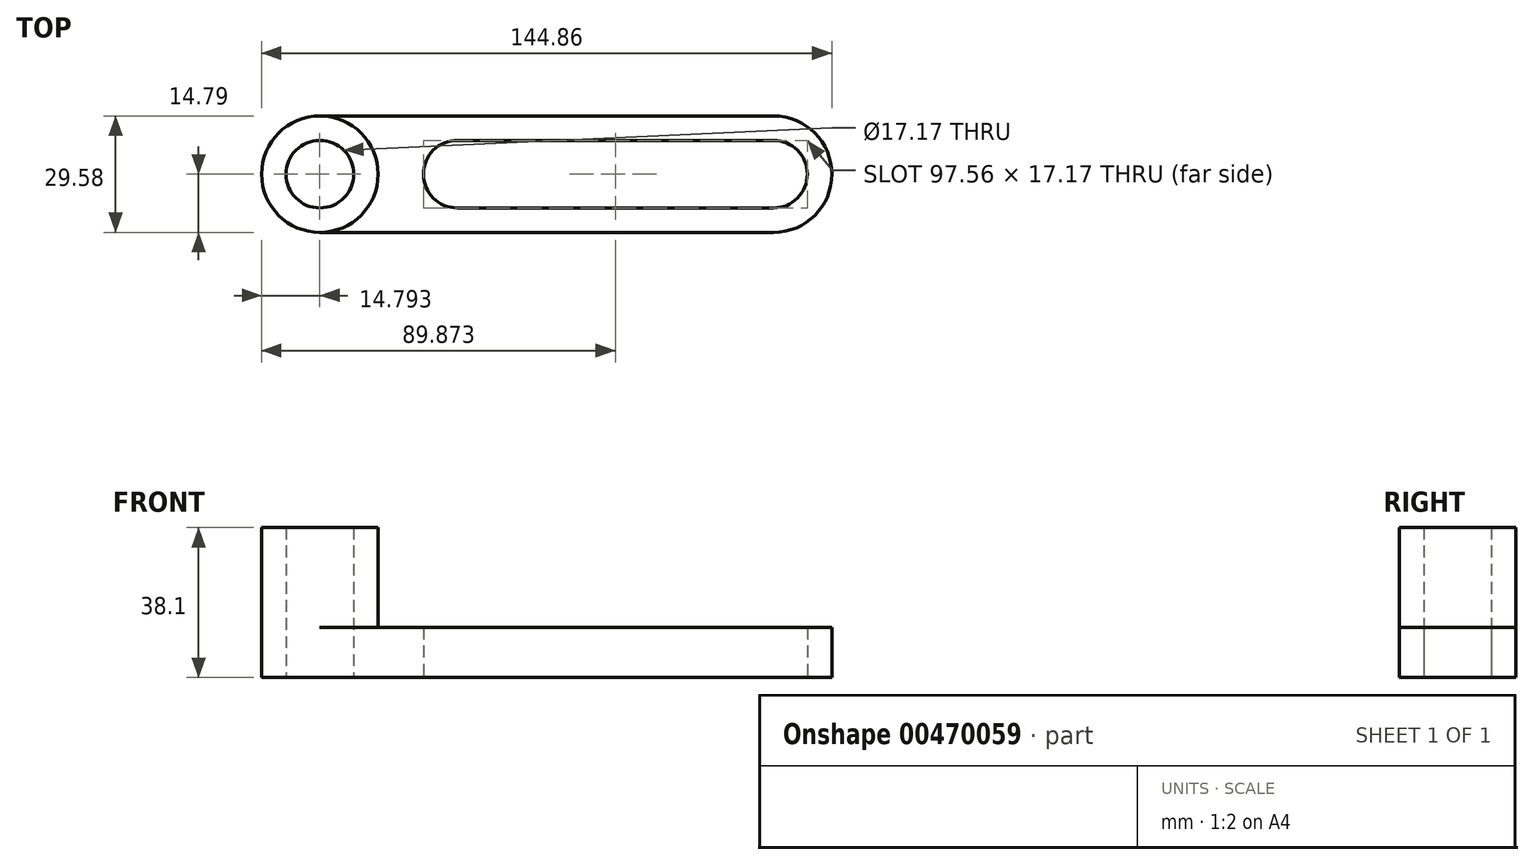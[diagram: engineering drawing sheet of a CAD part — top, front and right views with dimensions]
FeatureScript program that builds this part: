
annotation { "Feature Type Name" : "Feature", "Feature Type Description" : "" }
export const myFeature = defineFeature(function(context is Context, id is Id, definition is map)
    precondition{}
    {
        {
            var Q0;
            Q0=qCreatedBy(makeId("Top.planeOp"),FACE);
            var sketch = newSketch(context, id + "F0", { "sketchPlane" : qUnion([Q0])});
            skLineSegment(sketch, "E0.bottom", {"start": v(57.64, 14.79) * mm, "end": v(-57.64, 14.79) * mm});
            skLineSegment(sketch, "E0.top", {"start": v(57.64, -14.79) * mm, "end": v(-57.64, -14.79) * mm});
            skPoint(sketch, "E0.middle", {"position": v(0, 0) * mm});
            skArc(sketch, "E1", {"start": v(-57.64, 14.79) * mm, "mid": v(-72.43, 0) * mm, "end": v(-57.64, -14.79) * mm});
            skArc(sketch, "E2", {"start": v(57.64, 14.79) * mm, "mid": v(72.43, 0) * mm, "end": v(57.64, -14.79) * mm});
            skArc(sketch, "E3", {"start": v(-57.64, 14.79) * mm, "mid": v(-42.85, 0) * mm, "end": v(-57.64, -14.79) * mm});
            skLineSegment(sketch, "E4", {"start": v(0, 0) * mm, "end": v(-22.75, 0) * mm, "construction": true});
            skArc(sketch, "E5", {"start": v(-22.75, 8.58) * mm, "mid": v(-31.34, 0) * mm, "end": v(-22.75, -8.58) * mm});
            skArc(sketch, "E6", {"start": v(57.64, -8.58) * mm, "mid": v(66.22, 0) * mm, "end": v(57.64, 8.58) * mm});
            skLineSegment(sketch, "E7", {"start": v(-22.75, 8.58) * mm, "end": v(57.64, 8.58) * mm});
            skLineSegment(sketch, "E8", {"start": v(57.64, -8.58) * mm, "end": v(-22.75, -8.58) * mm});
            skCircle(sketch, "E9", {"center": v(-57.64, 0) * mm, "radius": 8.58 * mm});
            skSolve(sketch);
        }
        {
            var Q0;
            Q0=makeQuery(id+"F0.imprint","IMPRINT",FACE,{"disambiguationData":[TD([[makeQuery(id+"F0.imprint","IMPRINT",EDGE,{"derivedFrom":sQuery(id+"F0.wireOp",EDGE,"E0.bottom")}),1.0]])]});
            extrude(context, id + "F1", {"entities" : qUnion([Q0]), "depth" : 12.7 * mm});
        }
        {
            var Q0;
            Q0=makeQuery(id+"F0.imprint","IMPRINT",FACE,{"disambiguationData":[TD([[makeQuery(id+"F0.imprint","IMPRINT",EDGE,{"derivedFrom":sQuery(id+"F0.wireOp",EDGE,"E1")}),1.0]])]});
            extrude(context, id + "F2", {"entities" : qUnion([Q0]), "operationType" : NewBodyOperationType.ADD, "depth" : 38.1 * mm});
        }
    });
